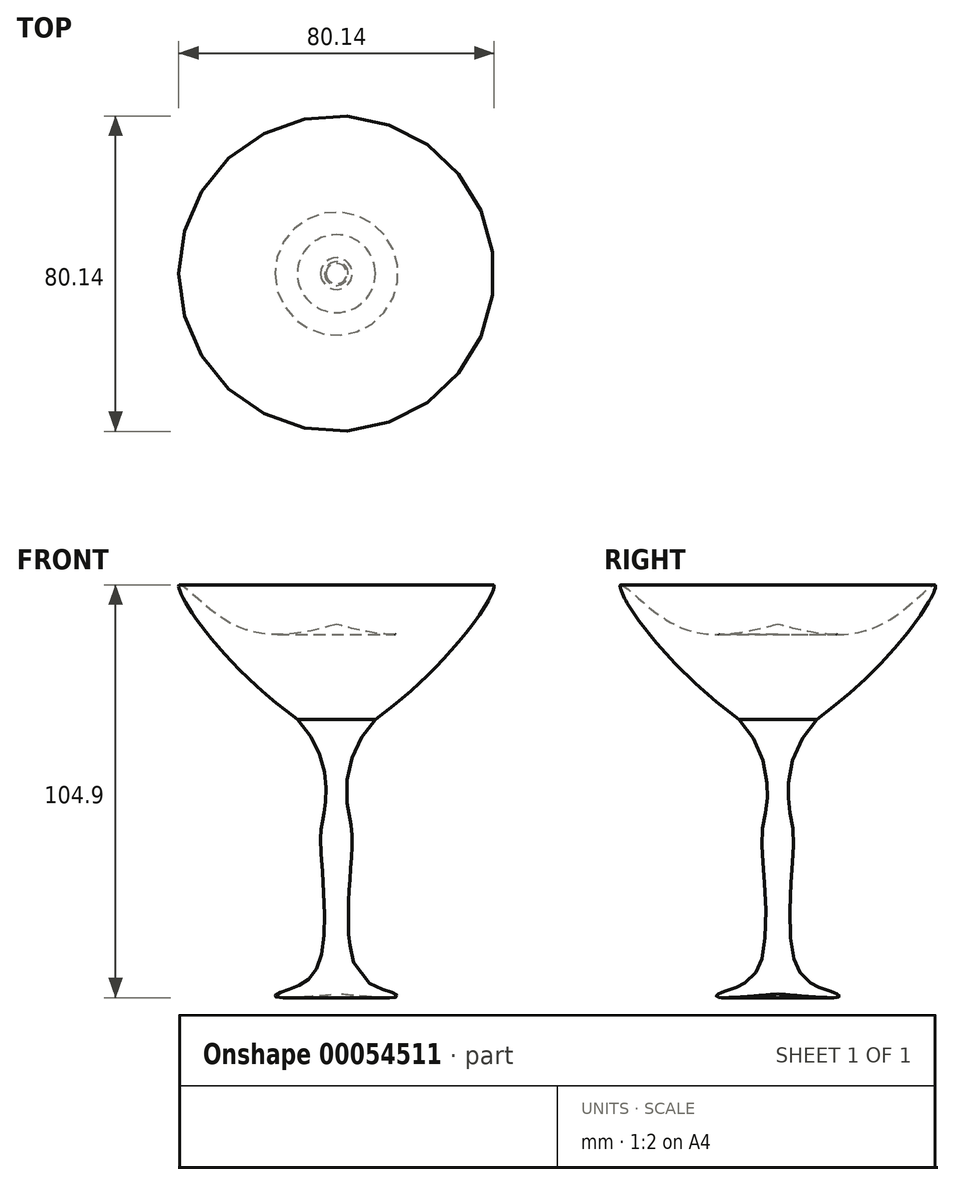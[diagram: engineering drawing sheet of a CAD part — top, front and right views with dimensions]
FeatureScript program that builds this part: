
annotation { "Feature Type Name" : "Feature", "Feature Type Description" : "" }
export const myFeature = defineFeature(function(context is Context, id is Id, definition is map)
    precondition{}
    {
        {
            var Q0;
            Q0=qCreatedBy(makeId("Front.planeOp"),FACE);
            var sketch = newSketch(context, id + "F0", { "sketchPlane" : qUnion([Q0])});
            skPoint(sketch, "E0.3.internal.orphan", {"position": v(-9.9, 0) * mm});
            skPoint(sketch, "E0.end.orphan", {"position": v(0, -24.03) * mm});
            skPoint(sketch, "E0.start.orphan", {"position": v(0, 24.13) * mm});
            skFitSpline(sketch, "E1", {"points": [v(0, 24.13) * mm, v(-26.39, 24.13) * mm, v(-39.8, 34.17) * mm, v(-9.9, 0) * mm], "startDerivative": vector(-87.05, -25.47) * mm, "endDerivative": vector(155.16, -112.9) * mm});
            skFitSpline(sketch, "E2", {"points": [v(-9.9, 0) * mm, v(-3.05, -23.6) * mm, v(-4.01, -30.95) * mm, v(-4.97, -63.26) * mm, v(-13.87, -69.31) * mm, v(-15.64, -70.44) * mm, v(0, -69.79) * mm], "startDerivative": vector(109.42, -115.22) * mm, "endDerivative": vector(130.17, 11.63) * mm});
            skLineSegment(sketch, "E3", {"start": v(0, 24.13) * mm, "end": v(0, -69.79) * mm});
            skLineSegment(sketch, "E4", {"start": v(0, -69.79) * mm, "end": v(0, 80.12) * mm});
            skSolve(sketch);
        }
        {
            var Q0;
            {var subQ0=sQuery(id+"F0.wireOp",EDGE,"E1");Q0=makeQuery(id+"F0.imprint","IMPRINT",FACE,{"disambiguationData":[TD([[makeQuery(id+"F0.imprint","IMPRINT",EDGE,{"derivedFrom":subQ0}),1.0]])]});}
            var Q1;
            Q1=sQuery(id+"F0.wireOp",EDGE,"E4");
            revolve(context, id + "F1", {"entities" : qUnion([Q0]), "axis" : qUnion([Q1]), "revolveType" : RevolveType.FULL});
        }
    });
